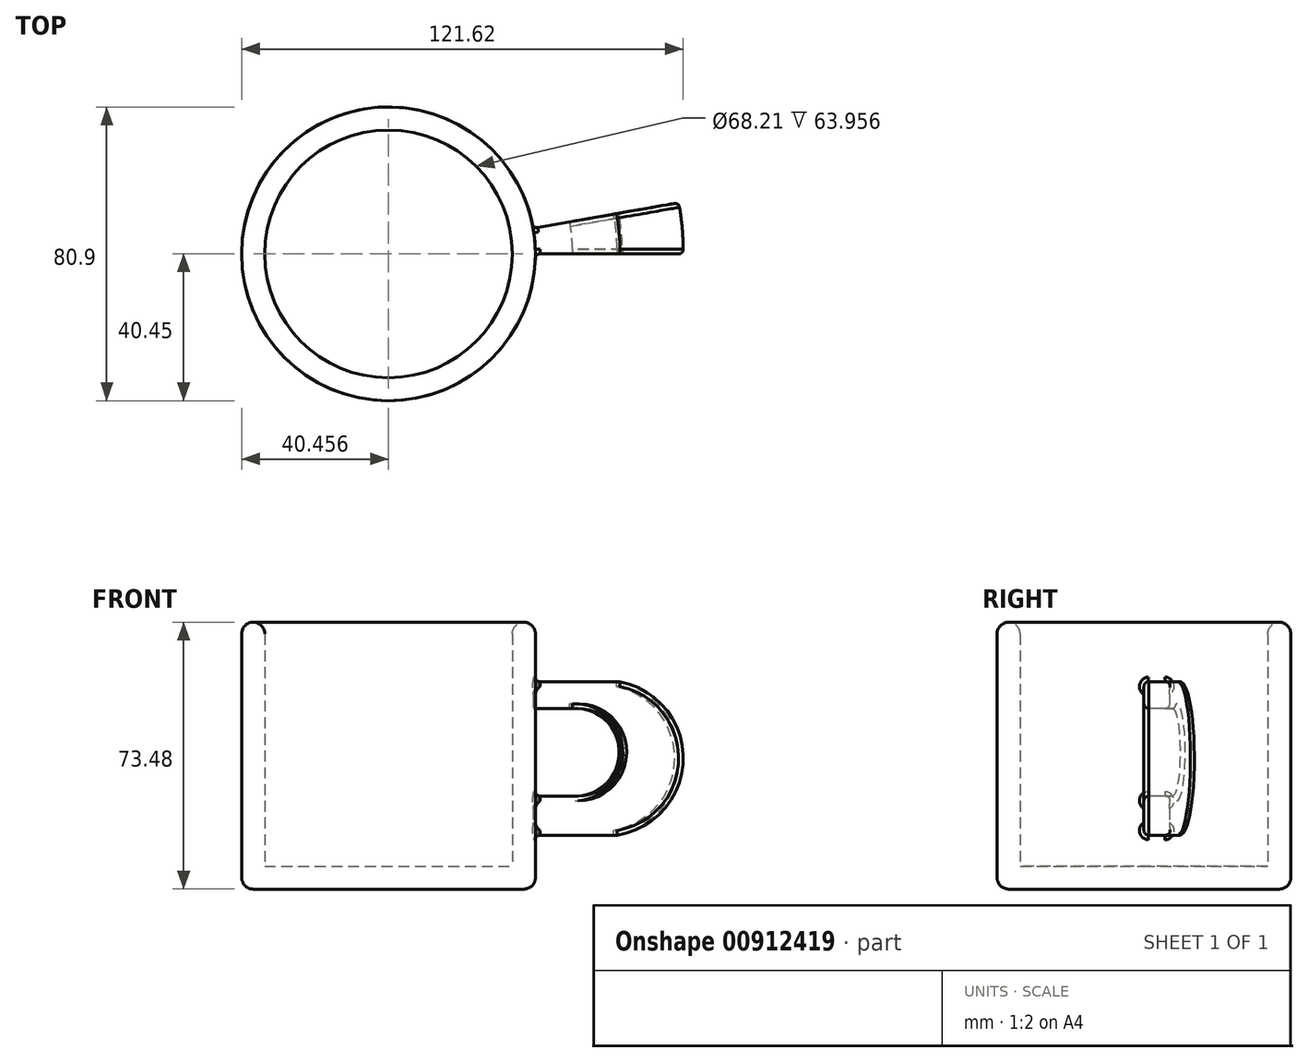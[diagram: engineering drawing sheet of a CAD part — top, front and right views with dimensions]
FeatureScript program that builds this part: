
annotation { "Feature Type Name" : "Feature", "Feature Type Description" : "" }
export const myFeature = defineFeature(function(context is Context, id is Id, definition is map)
    precondition{}
    {
        {
            var Q0;
            Q0=qCreatedBy(makeId("Front.planeOp"),FACE);
            var sketch = newSketch(context, id + "F0", { "sketchPlane" : qUnion([Q0])});
            skLineSegment(sketch, "E0.bottom", {"start": v(-43.65, 19.46) * mm, "end": v(-3.2, 19.46) * mm});
            skLineSegment(sketch, "E0.top", {"start": v(-43.65, -54.02) * mm, "end": v(-3.2, -54.02) * mm});
            skLineSegment(sketch, "E0.left", {"start": v(-43.65, 19.46) * mm, "end": v(-43.65, -54.02) * mm});
            skLineSegment(sketch, "E1", {"start": v(-3.2, 19.46) * mm, "end": v(-3.2, 3.07) * mm});
            skLineSegment(sketch, "E2", {"start": v(-3.2, -4.35) * mm, "end": v(-3.2, -28.42) * mm});
            skLineSegment(sketch, "E3", {"start": v(-3.2, -39.17) * mm, "end": v(-3.2, -54.02) * mm});
            skLineSegment(sketch, "E4", {"start": v(-3.2, 3.07) * mm, "end": v(20.1, 3.07) * mm});
            skLineSegment(sketch, "E5", {"start": v(-3.2, -39.17) * mm, "end": v(19.33, -39.17) * mm});
            skArc(sketch, "E6", {"start": v(19.33, -39.17) * mm, "mid": v(37.52, -18.37) * mm, "end": v(20.1, 3.07) * mm});
            skLineSegment(sketch, "E7", {"start": v(-3.2, -28.42) * mm, "end": v(8.58, -28.42) * mm});
            skLineSegment(sketch, "E8", {"start": v(-3.2, -4.35) * mm, "end": v(7.04, -4.35) * mm});
            skArc(sketch, "E9", {"start": v(8.58, -28.42) * mm, "mid": v(20.64, -15.57) * mm, "end": v(7.04, -4.35) * mm});
            skSolve(sketch);
        }
        {
            var Q0;
            Q0=makeQuery(id+"F0.imprint","IMPRINT",FACE,{"disambiguationData":[TD([[makeQuery(id+"F0.imprint","IMPRINT",EDGE,{"derivedFrom":sQuery(id+"F0.wireOp",EDGE,"E0.bottom")}),-1.0]])]});
            var Q1;
            Q1=sQuery(id+"F0.wireOp",EDGE,"E0.left");
            revolve(context, id + "F1", {"surfaceOperationType" : NewSurfaceOperationType.NEW, "entities" : qUnion([Q0]), "axis" : qUnion([Q1]), "revolveType" : RevolveType.ONE_DIRECTION, "oppositeDirection" : true, "angle" : 10 * degree});
        }
        {
            var Q0;
            Q0=makeQuery(id+"F1.opRevolve","CAP_FACE",FACE,{"disambiguationData":[OSD([sQuery(id+"F0.wireOp",EDGE,"E0.bottom"),sQuery(id+"F0.wireOp",EDGE,"E0.top"),sQuery(id+"F0.wireOp",EDGE,"E0.left"),sQuery(id+"F0.wireOp",EDGE,"E1"),sQuery(id+"F0.wireOp",EDGE,"E2"),sQuery(id+"F0.wireOp",EDGE,"E3"),sQuery(id+"F0.wireOp",EDGE,"E4"),sQuery(id+"F0.wireOp",EDGE,"E5"),sQuery(id+"F0.wireOp",EDGE,"E6"),sQuery(id+"F0.wireOp",EDGE,"E7"),sQuery(id+"F0.wireOp",EDGE,"E8"),sQuery(id+"F0.wireOp",EDGE,"E9")])],"isStart":true});
            var sketch = newSketch(context, id + "F2", { "sketchPlane" : qUnion([Q0])});
            skLineSegment(sketch, "E10.bottom", {"start": v(-43.65, 19.46) * mm, "end": v(-3.2, 19.46) * mm});
            skLineSegment(sketch, "E10.top", {"start": v(-43.65, -54.02) * mm, "end": v(-3.2, -54.02) * mm});
            skLineSegment(sketch, "E10.left", {"start": v(-43.65, 19.46) * mm, "end": v(-43.65, -54.02) * mm});
            skLineSegment(sketch, "E10.right", {"start": v(-3.2, 19.46) * mm, "end": v(-3.2, -54.02) * mm});
            skSolve(sketch);
        }
        {
            var Q0;
            {var subQ4=sQuery(id+"F2.wireOp",EDGE,"E10.bottom");Q0=makeQuery(id+"F2.imprint","IMPRINT",FACE,{"disambiguationData":[TD([[makeQuery(id+"F2.imprint","IMPRINT",EDGE,{"derivedFrom":subQ4}),-1.0]])]});}
            var Q1;
            Q1=sQuery(id+"F2.wireOp",EDGE,"E10.left");
            revolve(context, id + "F3", {"operationType" : NewBodyOperationType.ADD, "surfaceOperationType" : NewSurfaceOperationType.NEW, "entities" : qUnion([Q0]), "axis" : qUnion([Q1]), "revolveType" : RevolveType.ONE_DIRECTION, "angle" : 350 * degree});
        }
        {
            var Q0;
            Q0=makeQuery(id+"F3.boolean.opBoolean","MERGE",FACE,{"derivedFrom":[makeQuery(id+"F1.opRevolve","SWEPT_FACE",FACE,{"disambiguationData":[OSD([sQuery(id+"F0.wireOp",EDGE,"E0.bottom")])]}),makeQuery(id+"F3.opRevolve","SWEPT_FACE",FACE,{"disambiguationData":[OSD([sQuery(id+"F2.wireOp",EDGE,"E10.bottom")])]})]});
            shell(context, id + "F4", {"entities" : qUnion([Q0]), "thickness" : 6.35 * mm});
        }
        {
            var Q0;
            {var subQ2=sQuery(id+"F2.wireOp",EDGE,"E10.right");var subQ5=sQuery(id+"F0.wireOp",EDGE,"E4");Q0=makeQuery(id+"F3.boolean.opBoolean","SPLIT",EDGE,{"disambiguationData":[TD([makeQuery(id+"F1.opRevolve","SWEPT_FACE",FACE,{"disambiguationData":[OSD([subQ5])]})])],"derivedFrom":makeQuery(id+"F3.opRevolve","CAP_EDGE",EDGE,{"disambiguationData":[OSD([subQ2])],"isStart":false})});}
            var Q1;
            Q1=makeQuery(id+"F1.opRevolve","SWEPT_EDGE",EDGE,{"disambiguationData":[OSD([sQuery(id+"F0.wireOp",EDGE,"E2"),sQuery(id+"F0.wireOp",EDGE,"E7")])]});
            var Q2;
            {var subQ2=sQuery(id+"F2.wireOp",EDGE,"E10.right");var subQ5=sQuery(id+"F0.wireOp",EDGE,"E5");Q2=makeQuery(id+"F3.boolean.opBoolean","SPLIT",EDGE,{"disambiguationData":[TD([makeQuery(id+"F1.opRevolve","SWEPT_FACE",FACE,{"disambiguationData":[OSD([subQ5])]})])],"derivedFrom":makeQuery(id+"F3.opRevolve","CAP_EDGE",EDGE,{"disambiguationData":[OSD([subQ2])],"isStart":false})});}
            var Q3;
            Q3=makeQuery(id+"F1.opRevolve","CAP_EDGE",EDGE,{"disambiguationData":[OSD([sQuery(id+"F0.wireOp",EDGE,"E9")])],"isStart":false});
            var Q4;
            Q4=makeQuery(id+"F1.opRevolve","CAP_EDGE",EDGE,{"disambiguationData":[OSD([sQuery(id+"F0.wireOp",EDGE,"E7")])],"isStart":false});
            var Q5;
            Q5=makeQuery(id+"F1.opRevolve","CAP_EDGE",EDGE,{"disambiguationData":[OSD([sQuery(id+"F0.wireOp",EDGE,"E7")])],"isStart":true});
            var Q6;
            Q6=makeQuery(id+"F1.opRevolve","CAP_EDGE",EDGE,{"disambiguationData":[OSD([sQuery(id+"F0.wireOp",EDGE,"E8")])],"isStart":true});
            var Q7;
            {var subQ1=sQuery(id+"F2.wireOp",EDGE,"E10.right");var subQ5=sQuery(id+"F0.wireOp",EDGE,"E4");Q7=makeQuery(id+"F3.boolean.opBoolean","SPLIT",EDGE,{"disambiguationData":[TD([makeQuery(id+"F1.opRevolve","SWEPT_FACE",FACE,{"disambiguationData":[OSD([subQ5])]})])],"derivedFrom":makeQuery(id+"F3.opRevolve","CAP_EDGE",EDGE,{"disambiguationData":[OSD([subQ1])],"isStart":true})});}
            var Q8;
            Q8=makeQuery(id+"F1.opRevolve","SWEPT_EDGE",EDGE,{"disambiguationData":[OSD([sQuery(id+"F0.wireOp",EDGE,"E1"),sQuery(id+"F0.wireOp",EDGE,"E4")])]});
            var Q9;
            Q9=makeQuery(id+"F1.opRevolve","SWEPT_EDGE",EDGE,{"disambiguationData":[OSD([sQuery(id+"F0.wireOp",EDGE,"E3"),sQuery(id+"F0.wireOp",EDGE,"E5")])]});
            var Q10;
            Q10=makeQuery(id+"F1.opRevolve","CAP_EDGE",EDGE,{"disambiguationData":[OSD([sQuery(id+"F0.wireOp",EDGE,"E5")])],"isStart":false});
            var Q11;
            Q11=makeQuery(id+"F1.opRevolve","CAP_EDGE",EDGE,{"disambiguationData":[OSD([sQuery(id+"F0.wireOp",EDGE,"E5")])],"isStart":true});
            var Q12;
            Q12=makeQuery(id+"F1.opRevolve","CAP_EDGE",EDGE,{"disambiguationData":[OSD([sQuery(id+"F0.wireOp",EDGE,"E4")])],"isStart":true});
            var Q13;
            Q13=makeQuery(id+"F1.opRevolve","CAP_EDGE",EDGE,{"disambiguationData":[OSD([sQuery(id+"F0.wireOp",EDGE,"E4")])],"isStart":false});
            var Q14;
            Q14=makeQuery(id+"F1.opRevolve","CAP_EDGE",EDGE,{"disambiguationData":[OSD([sQuery(id+"F0.wireOp",EDGE,"E8")])],"isStart":false});
            var Q15;
            Q15=makeQuery(id+"F1.opRevolve","CAP_EDGE",EDGE,{"disambiguationData":[OSD([sQuery(id+"F0.wireOp",EDGE,"E6")])],"isStart":false});
            var Q16;
            Q16=makeQuery(id+"F1.opRevolve","CAP_EDGE",EDGE,{"disambiguationData":[OSD([sQuery(id+"F0.wireOp",EDGE,"E6")])],"isStart":true});
            fillet(context, id + "F5", {"entities" : qUnion([Q0, Q1, Q2, Q3, Q4, Q5, Q6, Q7, Q8, Q9, Q10, Q11, Q12, Q13, Q14, Q15, Q16]), "radius" : 1.27 * mm, "tangentPropagation" : true, "allowEdgeOverflow" : false});
        }
        {
            var Q0;
            Q0=makeQuery(id+"F3.boolean.opBoolean","MERGE",EDGE,{"derivedFrom":[makeQuery(id+"F1.opRevolve","SWEPT_EDGE",EDGE,{"disambiguationData":[OSD([sQuery(id+"F0.wireOp",EDGE,"E0.bottom"),sQuery(id+"F0.wireOp",EDGE,"E1")])]}),makeQuery(id+"F3.opRevolve","SWEPT_EDGE",EDGE,{"disambiguationData":[OSD([sQuery(id+"F2.wireOp",EDGE,"E10.bottom"),sQuery(id+"F2.wireOp",EDGE,"E10.right")])]})]});
            var Q1;
            Q1=makeQuery(id+"F4.opShell","OFFSET_EDGE",EDGE,{"disambiguationData":[OSD([sQuery(id+"F0.wireOp",EDGE,"E0.bottom"),sQuery(id+"F0.wireOp",EDGE,"E1"),sQuery(id+"F2.wireOp",EDGE,"E10.bottom"),sQuery(id+"F2.wireOp",EDGE,"E10.right")])]});
            var Q2;
            Q2=makeQuery(id+"F3.boolean.opBoolean","MERGE",EDGE,{"derivedFrom":[makeQuery(id+"F1.opRevolve","SWEPT_EDGE",EDGE,{"disambiguationData":[OSD([sQuery(id+"F0.wireOp",EDGE,"E0.top"),sQuery(id+"F0.wireOp",EDGE,"E3")])]}),makeQuery(id+"F3.opRevolve","SWEPT_EDGE",EDGE,{"disambiguationData":[OSD([sQuery(id+"F2.wireOp",EDGE,"E10.top"),sQuery(id+"F2.wireOp",EDGE,"E10.right")])]})]});
            fillet(context, id + "F6", {"entities" : qUnion([Q0, Q1, Q2]), "radius" : 3.17 * mm, "tangentPropagation" : true, "allowEdgeOverflow" : false});
        }
    });
